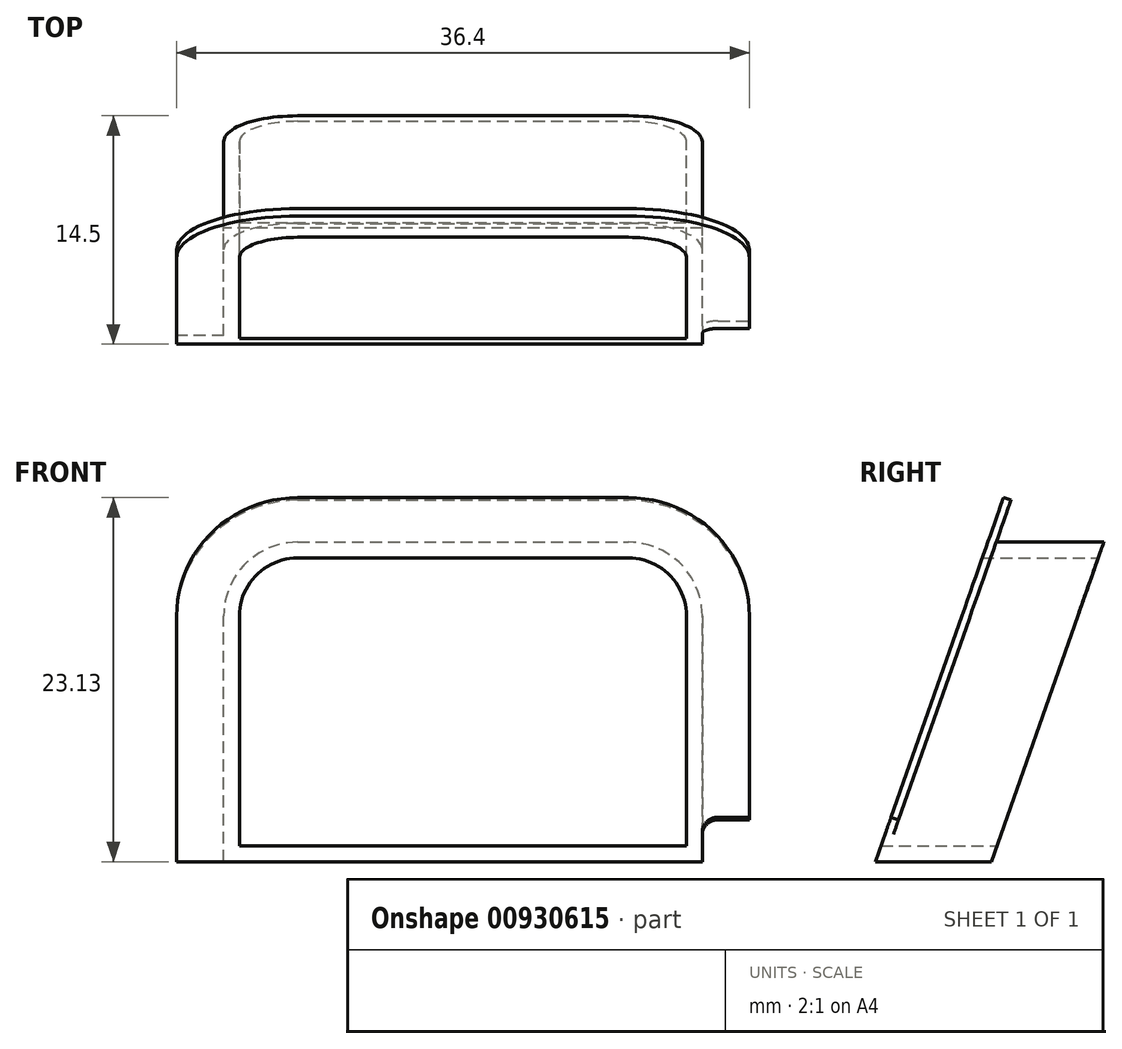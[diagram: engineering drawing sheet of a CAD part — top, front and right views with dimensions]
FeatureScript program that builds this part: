
annotation { "Feature Type Name" : "Feature", "Feature Type Description" : "" }
export const myFeature = defineFeature(function(context is Context, id is Id, definition is map)
    precondition{}
    {
        {
            var Q0;
            Q0=qCreatedBy(makeId("Front.planeOp"),FACE);
            var sketch = newSketch(context, id + "F0", { "sketchPlane" : qUnion([Q0])});
            skLineSegment(sketch, "E0.bottom", {"start": v(0, 0) * mm, "end": v(-31, 0) * mm, "construction": true});
            skLineSegment(sketch, "E0.top", {"start": v(0, 20.6) * mm, "end": v(-31, 20.6) * mm, "construction": true});
            skLineSegment(sketch, "E0.left", {"start": v(0, 0) * mm, "end": v(0, 20.6) * mm, "construction": true});
            skLineSegment(sketch, "E0.right", {"start": v(-31, 0) * mm, "end": v(-31, 20.6) * mm, "construction": true});
            skLineSegment(sketch, "E1.bottom", {"start": v(-30.7, 0) * mm, "end": v(-0.3, 0) * mm});
            skLineSegment(sketch, "E1.top", {"start": v(-26, 20.3) * mm, "end": v(-5, 20.3) * mm});
            skLineSegment(sketch, "E1.left", {"start": v(-30.7, 0) * mm, "end": v(-30.7, 15.6) * mm});
            skLineSegment(sketch, "E1.right", {"start": v(-0.3, 0) * mm, "end": v(-0.3, 15.6) * mm});
            skPoint(sketch, "E2.visualSharp", {"position": v(-30.7, 20.3) * mm});
            skArc(sketch, "E2.filletArc", {"start": v(-26, 20.3) * mm, "mid": v(-29.32, 18.92) * mm, "end": v(-30.7, 15.6) * mm});
            skPoint(sketch, "E3.visualSharp", {"position": v(-0.3, 20.3) * mm});
            skArc(sketch, "E3.filletArc", {"start": v(-0.3, 15.6) * mm, "mid": v(-1.68, 18.92) * mm, "end": v(-5, 20.3) * mm});
            skLineSegment(sketch, "E4", {"start": v(-29.7, 15.6) * mm, "end": v(-29.7, 1) * mm});
            skLineSegment(sketch, "E5", {"start": v(-29.7, 1) * mm, "end": v(-1.3, 1) * mm});
            skLineSegment(sketch, "E6", {"start": v(-1.3, 1) * mm, "end": v(-1.3, 15.6) * mm});
            skLineSegment(sketch, "E7", {"start": v(-26, 19.3) * mm, "end": v(-5, 19.3) * mm});
            skArc(sketch, "E8", {"start": v(-26, 19.3) * mm, "mid": v(-28.62, 18.22) * mm, "end": v(-29.7, 15.6) * mm});
            skArc(sketch, "E9", {"start": v(-1.3, 15.6) * mm, "mid": v(-2.38, 18.22) * mm, "end": v(-5, 19.3) * mm});
            skSolve(sketch);
        }
        {
            var Q0;
            Q0=qSketchRegion(id+"F0",true);
            extrude(context, id + "F1", {"entities" : qUnion([Q0]), "depth" : 14.5 * mm, "offsetDistance" : 25 * mm});
        }
        {
            var Q0;
            Q0=makeQuery(id+"F1.opExtrude","SWEPT_FACE",FACE,{"disambiguationData":[OSD([sQuery(id+"F0.wireOp",EDGE,"E1.left")])]});
            var sketch = newSketch(context, id + "F2", { "sketchPlane" : qUnion([Q0])});
            skLineSegment(sketch, "E10", {"start": v(14.5, 0) * mm, "end": v(7.36, 20.3) * mm});
            skLineSegment(sketch, "E11", {"start": v(7.36, 20.3) * mm, "end": v(14.5, 20.3) * mm});
            skLineSegment(sketch, "E12", {"start": v(14.5, 20.3) * mm, "end": v(14.5, 0) * mm});
            skLineSegment(sketch, "E13", {"start": v(0, 0) * mm, "end": v(7.14, 0) * mm});
            skLineSegment(sketch, "E14", {"start": v(7.14, 0) * mm, "end": v(0, 20.3) * mm});
            skLineSegment(sketch, "E15", {"start": v(0, 20.3) * mm, "end": v(0, 0) * mm});
            skSolve(sketch);
        }
        {
            var Q0;
            Q0=qSketchRegion(id+"F2",true);
            var Q1;
            Q1=makeQuery(id+"F1.opExtrude","SWEPT_FACE",FACE,{"disambiguationData":[OSD([sQuery(id+"F0.wireOp",EDGE,"E1.right")])]});
            extrude(context, id + "F3", {"entities" : qUnion([Q0]), "operationType" : NewBodyOperationType.REMOVE, "endBound" : BoundingType.UP_TO_SURFACE, "oppositeDirection" : true, "depth" : 25 * mm, "endBoundEntityFace" : qUnion([Q1]), "offsetDistance" : 25 * mm});
        }
        {
            var Q0;
            Q0=makeQuery(id+"F3.boolean.opBoolean","COPY",FACE,{"derivedFrom":makeQuery(id+"F3.opExtrude","SWEPT_FACE",FACE,{"disambiguationData":[OSD([sQuery(id+"F2.wireOp",EDGE,"E10")])]})});
            var sketch = newSketch(context, id + "F4", { "sketchPlane" : qUnion([Q0])});
            skLineSegment(sketch, "E16", {"start": v(-30.7, 11.73) * mm, "end": v(-30.7, -4.8) * mm});
            skLineSegment(sketch, "E17", {"start": v(-30.7, -4.8) * mm, "end": v(-33.7, -4.8) * mm});
            skLineSegment(sketch, "E18", {"start": v(-33.7, -4.8) * mm, "end": v(-33.7, 11.73) * mm});
            skEllipticalArc(sketch, "E19", {});
            skLineSegment(sketch, "E20", {"start": v(-26, 16.7) * mm, "end": v(-5, 16.7) * mm});
            skEllipticalArc(sketch, "E21", {});
            skEllipticalArc(sketch, "E22", {});
            skLineSegment(sketch, "E23", {"start": v(-26, 19.7) * mm, "end": v(-5, 19.7) * mm});
            skLineSegment(sketch, "E24", {"start": v(2.7, -1.8) * mm, "end": v(2.7, 11.73) * mm});
            skEllipticalArc(sketch, "E25", {});
            skLineSegment(sketch, "E26", {"start": v(0.7, -1.8) * mm, "end": v(2.7, -1.8) * mm});
            skArc(sketch, "E27", {"start": v(0.7, -1.8) * mm, "mid": v(0, -2.1) * mm, "end": v(-0.3, -2.8) * mm});
            skLineSegment(sketch, "E28", {"start": v(-0.3, 11.73) * mm, "end": v(-0.3, -2.8) * mm});
            const initialGuessF4  = {"E19": [-0.026, 0.011726501362467065, 0, 1, 0.0049820701242276645, 0.0047, 0, 1.5707963267948966], "E21": [-0.005, 0.011726501362467067, 0, 1, 0.004982070124227666, 0.0047, 4.71238898038469, 0], "E22": [-0.026, 0.011726501362467065, 0, 1, 0.00798207012422767, 0.0077, 0, 1.5707963267948966], "E25": [-0.005, 0.011726501362467067, 0, 1, 0.00798207012422768, 0.0077, 4.71238898038469, 0]};
            skSetInitialGuess(sketch, initialGuessF4);
            skSolve(sketch);
        }
        {
            var Q0;
            Q0=qSketchRegion(id+"F4",true);
            extrude(context, id + "F5", {"entities" : qUnion([Q0]), "operationType" : NewBodyOperationType.ADD, "oppositeDirection" : true, "depth" : 0.5 * mm, "offsetDistance" : 25 * mm});
        }
        {
            var Q0;
            Q0=makeQuery(id+"F5.opExtrude","SWEPT_FACE",FACE,{"disambiguationData":[OSD([sQuery(id+"F4.wireOp",EDGE,"E18")])]});
            var sketch = newSketch(context, id + "F6", { "sketchPlane" : qUnion([Q0])});
            skLineSegment(sketch, "E29", {"start": v(14.03, -0.17) * mm, "end": v(14.5, 0) * mm});
            skLineSegment(sketch, "E30", {"start": v(14.5, 0) * mm, "end": v(13.97, 0) * mm});
            skLineSegment(sketch, "E31", {"start": v(13.97, 0) * mm, "end": v(14.03, -0.17) * mm});
            skSolve(sketch);
        }
        {
            var Q0;
            Q0=qSketchRegion(id+"F6",true);
            var Q1;
            Q1=makeQuery(id+"F5.opExtrude","SWEPT_FACE",FACE,{"disambiguationData":[OSD([sQuery(id+"F4.wireOp",EDGE,"E24")])]});
            extrude(context, id + "F7", {"entities" : qUnion([Q0]), "operationType" : NewBodyOperationType.REMOVE, "endBound" : BoundingType.UP_TO_SURFACE, "oppositeDirection" : true, "depth" : 25 * mm, "endBoundEntityFace" : qUnion([Q1]), "offsetDistance" : 25 * mm});
        }
    });
